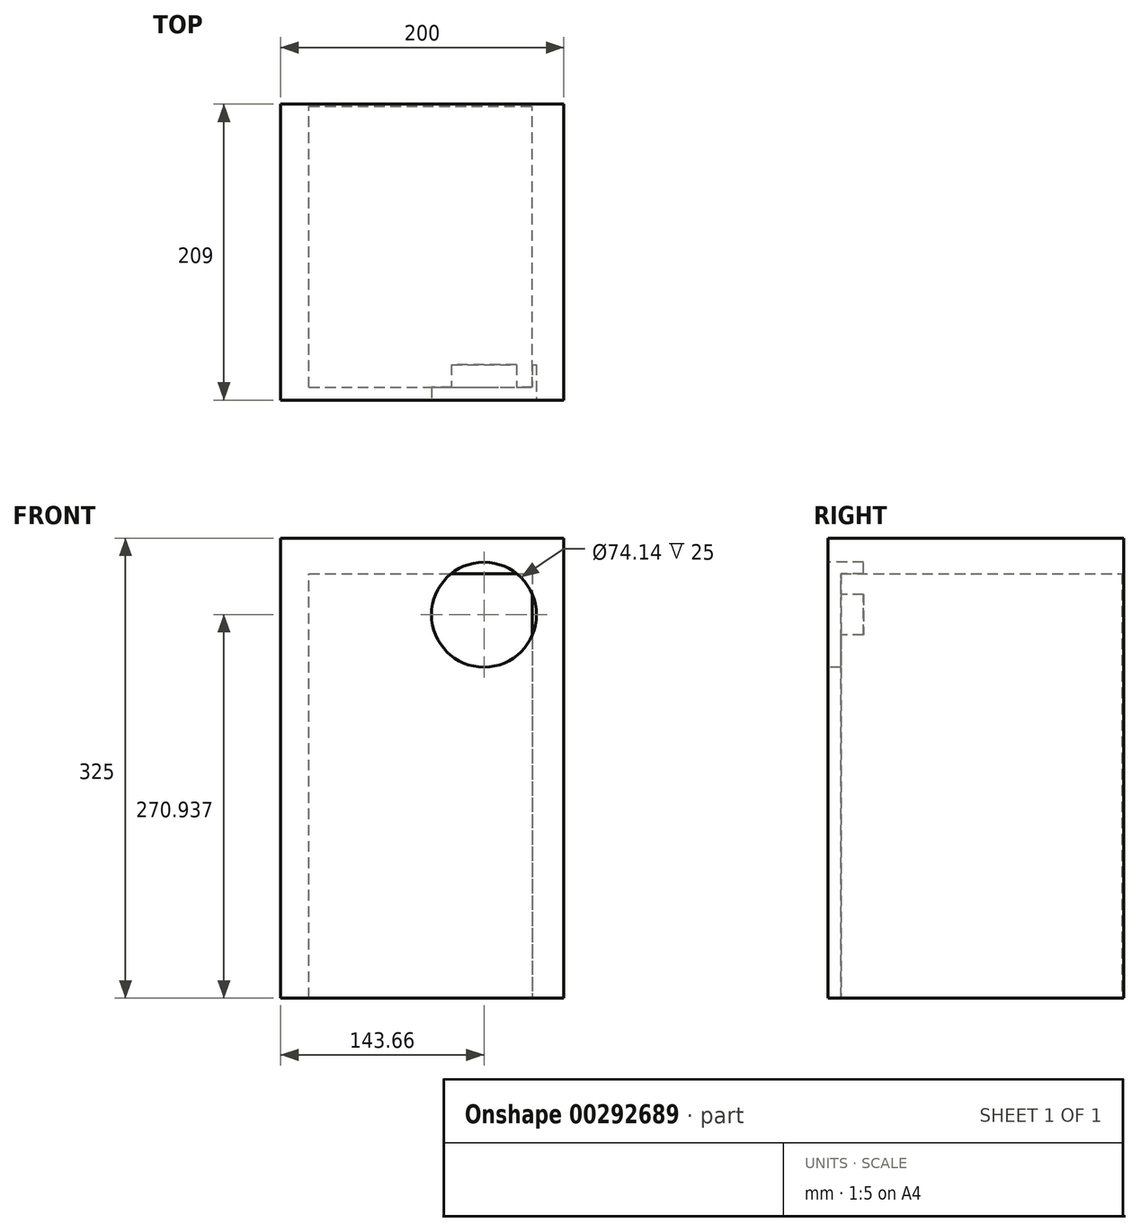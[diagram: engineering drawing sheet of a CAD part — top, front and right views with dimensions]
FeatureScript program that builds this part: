
annotation { "Feature Type Name" : "Feature", "Feature Type Description" : "" }
export const myFeature = defineFeature(function(context is Context, id is Id, definition is map)
    precondition{}
    {
        {
            var Q0;
            Q0=qCreatedBy(makeId("Front.planeOp"),FACE);
            var sketch = newSketch(context, id + "F0", { "sketchPlane" : qUnion([Q0])});
            skLineSegment(sketch, "E0.bottom", {"start": v(0, 0) * mm, "end": v(200, 0) * mm});
            skLineSegment(sketch, "E0.top", {"start": v(0, 300) * mm, "end": v(200, 300) * mm});
            skLineSegment(sketch, "E0.left", {"start": v(0, 0) * mm, "end": v(0, 300) * mm});
            skLineSegment(sketch, "E0.right", {"start": v(200, 0) * mm, "end": v(200, 300) * mm});
            skSolve(sketch);
        }
        {
            var Q0;
            Q0=makeQuery(id+"F0.imprint","IMPRINT",FACE,{"disambiguationData":[TD([[makeQuery(id+"F0.imprint","IMPRINT",EDGE,{"derivedFrom":sQuery(id+"F0.wireOp",EDGE,"E0.bottom")}),1.0]])]});
            var sketch = newSketch(context, id + "F1", { "sketchPlane" : qUnion([Q0])});
            skLineSegment(sketch, "E1.bottom", {"start": v(0, 0) * mm, "end": v(20, 0) * mm});
            skLineSegment(sketch, "E1.top", {"start": v(0, 300) * mm, "end": v(20, 300) * mm});
            skLineSegment(sketch, "E1.left", {"start": v(0, 0) * mm, "end": v(0, 300) * mm});
            skLineSegment(sketch, "E1.right", {"start": v(20, 0) * mm, "end": v(20, 300) * mm});
            skSolve(sketch);
        }
        {
            var Q0;
            Q0 = qSketchRegion(id + "F1", true);
            extrude(context, id + "F2", {"entities" : qUnion([Q0]), "depth" : 200 * mm});
        }
        {
            var Q0;
            Q0=makeQuery(id+"F0.imprint","IMPRINT",FACE,{"disambiguationData":[TD([[makeQuery(id+"F0.imprint","IMPRINT",EDGE,{"derivedFrom":sQuery(id+"F0.wireOp",EDGE,"E0.bottom")}),1.0]])]});
            var Q1;
            Q1 = qSketchRegion(id + "F1", true);
            extrude(context, id + "F3", {"entities" : qUnion([Q0, Q1]), "operationType" : NewBodyOperationType.ADD, "depth" : 1.5 * mm});
        }
        {
            var Q0;
            Q0=makeQuery(id+"F3.opExtrude","CAP_FACE",FACE,{"disambiguationData":[OSD([sQuery(id+"F0.wireOp",EDGE,"E0.bottom"),sQuery(id+"F0.wireOp",EDGE,"E0.top"),sQuery(id+"F0.wireOp",EDGE,"E0.left"),sQuery(id+"F0.wireOp",EDGE,"E0.right")])],"isStart":false});
            var sketch = newSketch(context, id + "F4", { "sketchPlane" : qUnion([Q0])});
            skLineSegment(sketch, "E2.bottom", {"start": v(177.85, 300) * mm, "end": v(200, 300) * mm});
            skLineSegment(sketch, "E2.top", {"start": v(177.85, 0) * mm, "end": v(200, 0) * mm});
            skLineSegment(sketch, "E2.left", {"start": v(177.85, 300) * mm, "end": v(177.85, 0) * mm});
            skLineSegment(sketch, "E2.right", {"start": v(200, 300) * mm, "end": v(200, 0) * mm});
            skSolve(sketch);
        }
        {
            var Q0;
            Q0=makeQuery(id+"F4.imprint","IMPRINT",FACE,{"disambiguationData":[TD([[makeQuery(id+"F4.imprint","IMPRINT",EDGE,{"derivedFrom":sQuery(id+"F4.wireOp",EDGE,"E2.bottom")}),-1.0]])]});
            extrude(context, id + "F5", {"entities" : qUnion([Q0]), "operationType" : NewBodyOperationType.ADD, "depth" : 200 * mm});
        }
        {
            var Q0;
            Q0=makeQuery(id+"F2.opExtrude","CAP_FACE",FACE,{"disambiguationData":[OSD([sQuery(id+"F1.wireOp",EDGE,"E1.bottom"),sQuery(id+"F1.wireOp",EDGE,"E1.top"),sQuery(id+"F1.wireOp",EDGE,"E1.left"),sQuery(id+"F1.wireOp",EDGE,"E1.right")])],"isStart":false});
            var sketch = newSketch(context, id + "F6", { "sketchPlane" : qUnion([Q0])});
            skLineSegment(sketch, "E3.bottom", {"start": v(0, 300) * mm, "end": v(200, 300) * mm});
            skLineSegment(sketch, "E3.top", {"start": v(0, 0) * mm, "end": v(200, 0) * mm});
            skLineSegment(sketch, "E3.left", {"start": v(0, 300) * mm, "end": v(0, 0) * mm});
            skLineSegment(sketch, "E3.right", {"start": v(200, 300) * mm, "end": v(200, 0) * mm});
            skSolve(sketch);
        }
        {
            var Q0;
            Q0 = qSketchRegion(id + "F6", true);
            extrude(context, id + "F7", {"entities" : qUnion([Q0]), "operationType" : NewBodyOperationType.ADD, "depth" : 9 * mm});
        }
        {
            var Q0;
            Q0=makeQuery(id+"F7.boolean.opBoolean","MERGE",FACE,{"derivedFrom":[makeQuery(id+"F5.boolean.opBoolean","MERGE",FACE,{"derivedFrom":[makeQuery(id+"F3.boolean.opBoolean","MERGE",FACE,{"derivedFrom":[makeQuery(id+"F2.opExtrude","SWEPT_FACE",FACE,{"disambiguationData":[OSD([sQuery(id+"F1.wireOp",EDGE,"E1.top")])]}),makeQuery(id+"F3.opExtrude","SWEPT_FACE",FACE,{"disambiguationData":[OSD([sQuery(id+"F0.wireOp",EDGE,"E0.top")])]})]}),makeQuery(id+"F5.opExtrude","SWEPT_FACE",FACE,{"disambiguationData":[OSD([sQuery(id+"F4.wireOp",EDGE,"E2.bottom")])]})]}),makeQuery(id+"F7.opExtrude","SWEPT_FACE",FACE,{"disambiguationData":[OSD([sQuery(id+"F6.wireOp",EDGE,"E3.bottom")])]})]});
            var sketch = newSketch(context, id + "F8", { "sketchPlane" : qUnion([Q0])});
            skLineSegment(sketch, "E4.bottom", {"start": v(0, -209) * mm, "end": v(200, -209) * mm});
            skLineSegment(sketch, "E4.top", {"start": v(0, 0) * mm, "end": v(200, 0) * mm});
            skLineSegment(sketch, "E4.left", {"start": v(0, -209) * mm, "end": v(0, 0) * mm});
            skLineSegment(sketch, "E4.right", {"start": v(200, -209) * mm, "end": v(200, 0) * mm});
            skSolve(sketch);
        }
        {
            var Q0;
            Q0 = qSketchRegion(id + "F8", true);
            extrude(context, id + "F9", {"entities" : qUnion([Q0]), "operationType" : NewBodyOperationType.ADD, "depth" : 25 * mm});
        }
        {
            var Q0;
            Q0=makeQuery(id+"F9.boolean.opBoolean","MERGE",FACE,{"derivedFrom":[makeQuery(id+"F7.opExtrude","CAP_FACE",FACE,{"disambiguationData":[OSD([sQuery(id+"F6.wireOp",EDGE,"E3.bottom"),sQuery(id+"F6.wireOp",EDGE,"E3.top"),sQuery(id+"F6.wireOp",EDGE,"E3.left"),sQuery(id+"F6.wireOp",EDGE,"E3.right")])],"isStart":false}),makeQuery(id+"F9.opExtrude","SWEPT_FACE",FACE,{"disambiguationData":[OSD([sQuery(id+"F8.wireOp",EDGE,"E4.bottom")])]})]});
            var sketch = newSketch(context, id + "F10", { "sketchPlane" : qUnion([Q0])});
            skCircle(sketch, "E5", {"center": v(143.66, 270.94) * mm, "radius": 37.07 * mm});
            skSolve(sketch);
        }
        {
            var Q0;
            Q0=makeQuery(id+"F10.imprint","IMPRINT",FACE,{"disambiguationData":[TD([[makeQuery(id+"F10.imprint","IMPRINT",EDGE,{"derivedFrom":sQuery(id+"F10.wireOp",EDGE,"E5")}),1.0]])]});
            extrude(context, id + "F11", {"entities" : qUnion([Q0]), "operationType" : NewBodyOperationType.REMOVE, "oppositeDirection" : true, "depth" : 25 * mm});
        }
    });
